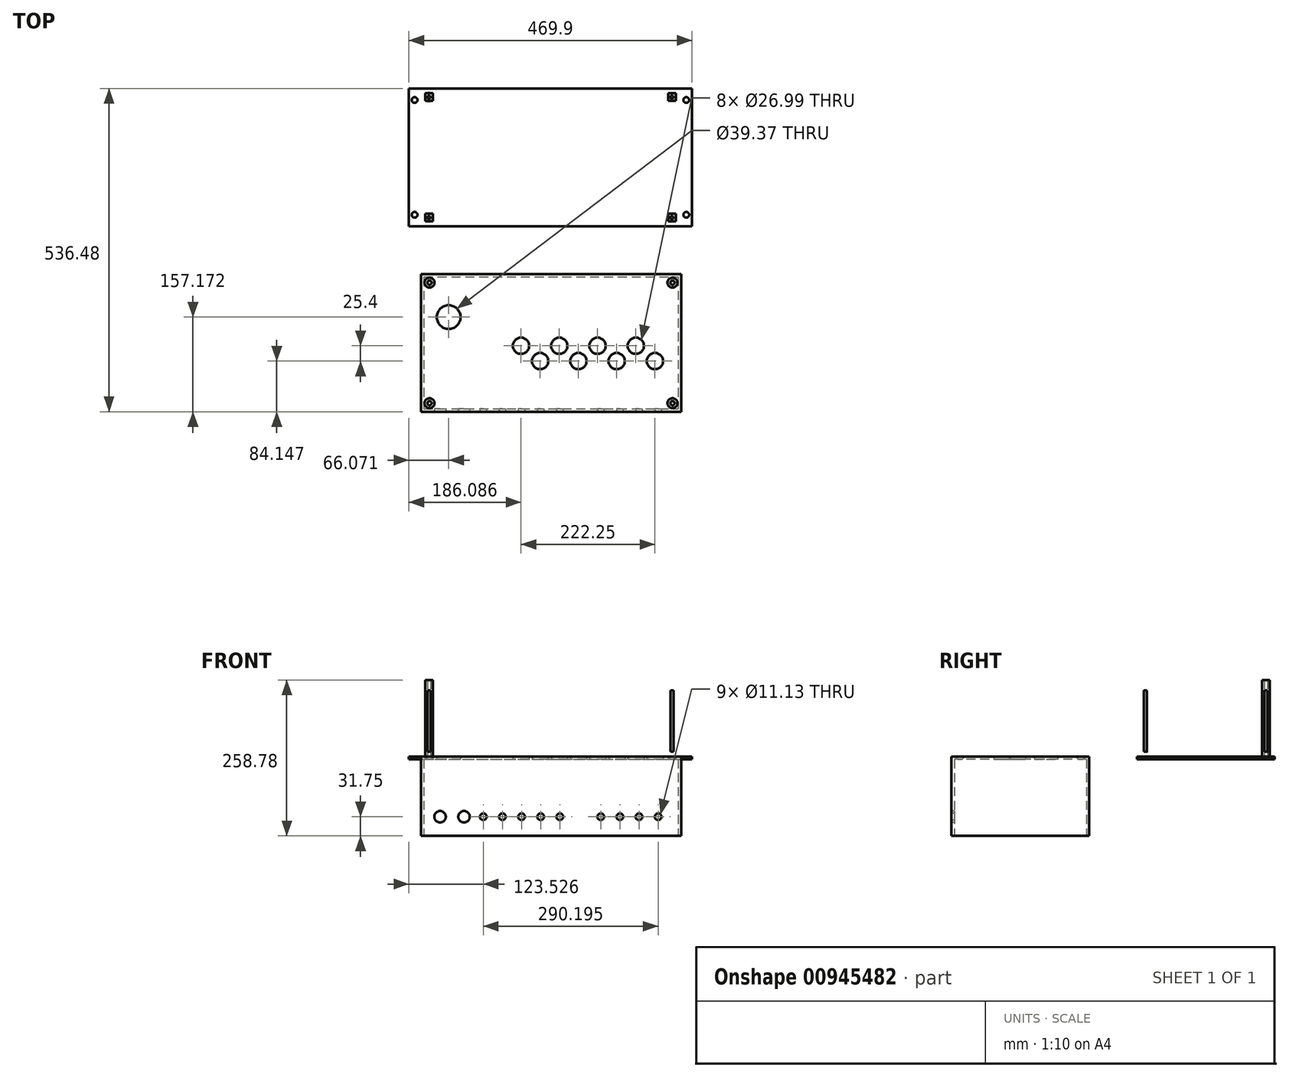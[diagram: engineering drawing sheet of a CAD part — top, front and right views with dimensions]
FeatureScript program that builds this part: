
annotation { "Feature Type Name" : "Feature", "Feature Type Description" : "" }
export const myFeature = defineFeature(function(context is Context, id is Id, definition is map)
    precondition{}
    {
        {
            var Q0;
            Q0=qCreatedBy(makeId("Top.planeOp"),FACE);
            var sketch = newSketch(context, id + "F0", { "sketchPlane" : qUnion([Q0])});
            skLineSegment(sketch, "E0.bottom", {"start": v(-225.5, 123.74) * mm, "end": v(206.3, 123.74) * mm});
            skLineSegment(sketch, "E0.top", {"start": v(-225.5, -104.86) * mm, "end": v(206.3, -104.86) * mm});
            skLineSegment(sketch, "E0.left", {"start": v(-225.5, 123.74) * mm, "end": v(-225.5, -104.86) * mm});
            skLineSegment(sketch, "E0.right", {"start": v(206.3, 123.74) * mm, "end": v(206.3, -104.86) * mm});
            skLineSegment(sketch, "E1.bottom", {"start": v(-220.72, 118.97) * mm, "end": v(201.56, 118.97) * mm});
            skLineSegment(sketch, "E1.top", {"start": v(-220.72, -100.1) * mm, "end": v(201.56, -100.1) * mm});
            skLineSegment(sketch, "E1.left", {"start": v(-220.72, 118.97) * mm, "end": v(-220.72, -100.1) * mm});
            skLineSegment(sketch, "E1.right", {"start": v(201.56, 118.97) * mm, "end": v(201.56, -100.1) * mm});
            skLineSegment(sketch, "E2.bottom", {"start": v(-225.5, 123.74) * mm, "end": v(-244.54, 123.74) * mm});
            skLineSegment(sketch, "E2.top", {"start": v(-225.5, -104.86) * mm, "end": v(-244.54, -104.86) * mm});
            skLineSegment(sketch, "E2.right", {"start": v(-244.54, 123.74) * mm, "end": v(-244.54, -104.86) * mm});
            skLineSegment(sketch, "E3.bottom", {"start": v(206.3, 123.74) * mm, "end": v(225.36, 123.74) * mm});
            skLineSegment(sketch, "E3.top", {"start": v(206.3, -104.86) * mm, "end": v(225.36, -104.86) * mm});
            skLineSegment(sketch, "E3.right", {"start": v(225.36, 123.74) * mm, "end": v(225.36, -104.86) * mm});
            skCircle(sketch, "E4", {"center": v(-235.02, 104.69) * mm, "radius": 4.76 * mm});
            skCircle(sketch, "E5", {"center": v(-235.02, -85.81) * mm, "radius": 4.76 * mm});
            skCircle(sketch, "E6", {"center": v(215.83, 104.69) * mm, "radius": 4.76 * mm});
            skCircle(sketch, "E7", {"center": v(215.83, -85.81) * mm, "radius": 4.76 * mm});
            skLineSegment(sketch, "E8.bottom", {"start": v(-219.74, -188.9) * mm, "end": v(202.53, -188.9) * mm});
            skLineSegment(sketch, "E8.top", {"start": v(-219.74, -407.97) * mm, "end": v(202.53, -407.97) * mm});
            skLineSegment(sketch, "E8.left", {"start": v(-219.74, -188.9) * mm, "end": v(-219.74, -407.97) * mm});
            skLineSegment(sketch, "E8.right", {"start": v(202.53, -188.9) * mm, "end": v(202.53, -407.97) * mm});
            skCircle(sketch, "E9", {"center": v(-58.45, -303.2) * mm, "radius": 13.5 * mm});
            skCircle(sketch, "E10", {"center": v(-26.7, -328.6) * mm, "radius": 13.5 * mm});
            skCircle(sketch, "E11", {"center": v(5.05, -303.2) * mm, "radius": 13.5 * mm});
            skCircle(sketch, "E12", {"center": v(163.8, -328.6) * mm, "radius": 13.5 * mm});
            skCircle(sketch, "E13", {"center": v(100.3, -328.6) * mm, "radius": 13.5 * mm});
            skCircle(sketch, "E14", {"center": v(68.55, -303.2) * mm, "radius": 13.5 * mm});
            skCircle(sketch, "E15", {"center": v(36.8, -328.6) * mm, "radius": 13.5 * mm});
            skCircle(sketch, "E16", {"center": v(132.05, -303.2) * mm, "radius": 13.5 * mm});
            skCircle(sketch, "E17", {"center": v(-178.47, -255.57) * mm, "radius": 19.69 * mm});
            skCircle(sketch, "E18", {"center": v(-210.22, -198.42) * mm, "radius": 3.18 * mm});
            skLineSegment(sketch, "E19.bottom", {"start": v(-217.54, -84.23) * mm, "end": v(-204.84, -84.23) * mm});
            skLineSegment(sketch, "E19.top", {"start": v(-217.54, -96.93) * mm, "end": v(-204.84, -96.93) * mm});
            skLineSegment(sketch, "E19.left", {"start": v(-217.54, -84.23) * mm, "end": v(-217.54, -96.93) * mm});
            skLineSegment(sketch, "E19.right", {"start": v(-204.84, -84.23) * mm, "end": v(-204.84, -96.93) * mm});
            skLineSegment(sketch, "E20.bottom", {"start": v(185.68, -84.23) * mm, "end": v(198.38, -84.23) * mm});
            skLineSegment(sketch, "E20.top", {"start": v(185.68, -96.93) * mm, "end": v(198.38, -96.93) * mm});
            skLineSegment(sketch, "E20.left", {"start": v(185.68, -84.23) * mm, "end": v(185.68, -96.93) * mm});
            skLineSegment(sketch, "E20.right", {"start": v(198.38, -84.23) * mm, "end": v(198.38, -96.93) * mm});
            skLineSegment(sketch, "E21.bottom", {"start": v(185.68, 115.8) * mm, "end": v(198.38, 115.8) * mm});
            skLineSegment(sketch, "E21.top", {"start": v(185.68, 103.1) * mm, "end": v(198.38, 103.1) * mm});
            skLineSegment(sketch, "E21.left", {"start": v(185.68, 115.8) * mm, "end": v(185.68, 103.1) * mm});
            skLineSegment(sketch, "E21.right", {"start": v(198.38, 115.8) * mm, "end": v(198.38, 103.1) * mm});
            skLineSegment(sketch, "E22.bottom", {"start": v(-217.54, 115.8) * mm, "end": v(-204.84, 115.8) * mm});
            skLineSegment(sketch, "E22.top", {"start": v(-217.54, 103.1) * mm, "end": v(-204.84, 103.1) * mm});
            skLineSegment(sketch, "E22.left", {"start": v(-217.54, 115.8) * mm, "end": v(-217.54, 103.1) * mm});
            skLineSegment(sketch, "E22.right", {"start": v(-204.84, 115.8) * mm, "end": v(-204.84, 103.1) * mm});
            skCircle(sketch, "E23", {"center": v(-210.22, -398.44) * mm, "radius": 3.18 * mm});
            skCircle(sketch, "E24", {"center": v(193, -398.44) * mm, "radius": 3.18 * mm});
            skCircle(sketch, "E25", {"center": v(193, -198.42) * mm, "radius": 3.18 * mm});
            skLineSegment(sketch, "E26.bottom", {"start": v(-224.52, -184.14) * mm, "end": v(207.28, -184.14) * mm});
            skLineSegment(sketch, "E26.top", {"start": v(-224.52, -412.74) * mm, "end": v(207.28, -412.74) * mm});
            skLineSegment(sketch, "E26.left", {"start": v(-224.52, -184.14) * mm, "end": v(-224.52, -412.74) * mm});
            skLineSegment(sketch, "E26.right", {"start": v(207.28, -184.14) * mm, "end": v(207.28, -412.74) * mm});
            skCircle(sketch, "E27", {"center": v(-211.2, 109.45) * mm, "radius": 2.58 * mm});
            skCircle(sketch, "E28", {"center": v(192.03, 109.45) * mm, "radius": 2.58 * mm});
            skCircle(sketch, "E29", {"center": v(192.03, -90.58) * mm, "radius": 2.58 * mm});
            skCircle(sketch, "E30", {"center": v(-211.2, -90.58) * mm, "radius": 2.58 * mm});
            skSolve(sketch);
        }
        {
            var Q0;
            Q0=makeQuery(id+"F0.imprint","IMPRINT",FACE,{"disambiguationData":[TD([[makeQuery(id+"F0.imprint","IMPRINT",EDGE,{"derivedFrom":sQuery(id+"F0.wireOp",EDGE,"E1.bottom")}),-1.0]])]});
            var Q1;
            Q1=makeQuery(id+"F0.imprint","IMPRINT",FACE,{"disambiguationData":[TD([[makeQuery(id+"F0.imprint","IMPRINT",EDGE,{"derivedFrom":sQuery(id+"F0.wireOp",EDGE,"E0.bottom")}),-1.0]])]});
            extrude(context, id + "F1", {"entities" : qUnion([Q0, Q1]), "depth" : 4.78 * mm, "offsetDistance" : 25.4 * mm});
        }
        {
            var Q0;
            Q0=makeQuery(id+"F0.imprint","IMPRINT",FACE,{"disambiguationData":[TD([[makeQuery(id+"F0.imprint","IMPRINT",EDGE,{"derivedFrom":sQuery(id+"F0.wireOp",EDGE,"E2.bottom")}),1.0]])]});
            var Q1;
            Q1=makeQuery(id+"F0.imprint","IMPRINT",FACE,{"disambiguationData":[TD([[makeQuery(id+"F0.imprint","IMPRINT",EDGE,{"derivedFrom":sQuery(id+"F0.wireOp",EDGE,"E3.bottom")}),-1.0]])]});
            extrude(context, id + "F2", {"entities" : qUnion([Q0, Q1]), "operationType" : NewBodyOperationType.ADD, "depth" : 4.78 * mm, "offsetDistance" : 25.4 * mm});
        }
        {
            var Q0;
            Q0=makeQuery(id+"F0.imprint","IMPRINT",FACE,{"disambiguationData":[TD([[makeQuery(id+"F0.imprint","IMPRINT",EDGE,{"derivedFrom":sQuery(id+"F0.wireOp",EDGE,"E8.bottom")}),-1.0]])]});
            extrude(context, id + "F3", {"entities" : qUnion([Q0]), "depth" : 4.78 * mm, "offsetDistance" : 25.4 * mm});
        }
        {
            var Q0;
            Q0=makeQuery(id+"F0.imprint","IMPRINT",FACE,{"disambiguationData":[TD([[makeQuery(id+"F0.imprint","IMPRINT",EDGE,{"derivedFrom":sQuery(id+"F0.wireOp",EDGE,"E8.bottom")}),1.0]])]});
            extrude(context, id + "F4", {"entities" : qUnion([Q0]), "operationType" : NewBodyOperationType.ADD, "depth" : 4.78 * mm, "offsetDistance" : 25.4 * mm, "hasSecondDirection" : true, "secondDirectionOppositeDirection" : true, "secondDirectionDepth" : 127 * mm});
        }
        {
            var Q0;
            Q0=makeQuery(id+"F4.opExtrude","SWEPT_FACE",FACE,{"disambiguationData":[OSD([sQuery(id+"F0.wireOp",EDGE,"E26.top")])]});
            var sketch = newSketch(context, id + "F5", { "sketchPlane" : qUnion([Q0])});
            skCircle(sketch, "E31", {"center": v(-192.77, -95.25) * mm, "radius": 9.53 * mm});
            skCircle(sketch, "E32", {"center": v(-153.07, -95.25) * mm, "radius": 9.53 * mm});
            skCircle(sketch, "E33", {"center": v(-89.26, -95.25) * mm, "radius": 5.56 * mm});
            skCircle(sketch, "E34", {"center": v(-57.51, -95.25) * mm, "radius": 5.56 * mm});
            skCircle(sketch, "E35", {"center": v(-25.76, -95.25) * mm, "radius": 5.56 * mm});
            skPoint(sketch, "E36", {"position": v(5.99, -95.25) * mm});
            skCircle(sketch, "E37", {"center": v(5.99, -95.25) * mm, "radius": 5.56 * mm});
            skCircle(sketch, "E38", {"center": v(73.93, -95.25) * mm, "radius": 5.56 * mm});
            skCircle(sketch, "E39", {"center": v(105.68, -95.25) * mm, "radius": 5.56 * mm});
            skCircle(sketch, "E40", {"center": v(137.43, -95.25) * mm, "radius": 5.56 * mm});
            skCircle(sketch, "E41", {"center": v(169.18, -95.25) * mm, "radius": 5.56 * mm});
            skCircle(sketch, "E42", {"center": v(-121.01, -95.25) * mm, "radius": 5.56 * mm});
            skSolve(sketch);
        }
        {
            var Q0;
            Q0=sQuery(id+"F5.wireOp",VERTEX,"E31.center");
            var Q1;
            Q1=sQuery(id+"F5.wireOp",VERTEX,"E32.center");
            var Q2;
            Q2=makeQuery(id+"F3.opExtrude","SWEPT_BODY",BODY,{"disambiguationData":[OSD([sQuery(id+"F0.wireOp",EDGE,"E8.bottom"),sQuery(id+"F0.wireOp",EDGE,"E8.top"),sQuery(id+"F0.wireOp",EDGE,"E8.left"),sQuery(id+"F0.wireOp",EDGE,"E8.right"),sQuery(id+"F0.wireOp",EDGE,"E9"),sQuery(id+"F0.wireOp",EDGE,"E10"),sQuery(id+"F0.wireOp",EDGE,"E11"),sQuery(id+"F0.wireOp",EDGE,"E12"),sQuery(id+"F0.wireOp",EDGE,"E13"),sQuery(id+"F0.wireOp",EDGE,"E14"),sQuery(id+"F0.wireOp",EDGE,"E15"),sQuery(id+"F0.wireOp",EDGE,"E16"),sQuery(id+"F0.wireOp",EDGE,"E17"),sQuery(id+"F0.wireOp",EDGE,"E18"),sQuery(id+"F0.wireOp",EDGE,"E23"),sQuery(id+"F0.wireOp",EDGE,"E24"),sQuery(id+"F0.wireOp",EDGE,"E25")])]});
            hole(context, id + "F6", {"style" : HoleStyle.SIMPLE, "endStyle" : HoleEndStyle.BLIND, "holeDiameter" : 19.05 * mm, "majorDiameter" : 6.35 * mm, "holeDepth" : 12.7 * mm, "isTappedThrough" : true, "tappedDepth" : 12.7 * mm, "tapClearance" : 3, "locations" : qUnion([Q0, Q1]), "scope" : qUnion([Q2])});
        }
        {
            var Q0;
            Q0=sQuery(id+"F5.wireOp",VERTEX,"E33.center");
            var Q1;
            Q1=sQuery(id+"F5.wireOp",VERTEX,"E34.center");
            var Q2;
            Q2=sQuery(id+"F5.wireOp",VERTEX,"E35.center");
            var Q3;
            Q3=sQuery(id+"F5.wireOp",VERTEX,"E36");
            var Q4;
            Q4=sQuery(id+"F5.wireOp",VERTEX,"E38.center");
            var Q5;
            Q5=sQuery(id+"F5.wireOp",VERTEX,"E39.center");
            var Q6;
            Q6=sQuery(id+"F5.wireOp",VERTEX,"E40.center");
            var Q7;
            Q7=sQuery(id+"F5.wireOp",VERTEX,"E41.center");
            var Q8;
            Q8=makeQuery(id+"F3.opExtrude","SWEPT_BODY",BODY,{"disambiguationData":[OSD([sQuery(id+"F0.wireOp",EDGE,"E8.bottom"),sQuery(id+"F0.wireOp",EDGE,"E8.top"),sQuery(id+"F0.wireOp",EDGE,"E8.left"),sQuery(id+"F0.wireOp",EDGE,"E8.right"),sQuery(id+"F0.wireOp",EDGE,"E9"),sQuery(id+"F0.wireOp",EDGE,"E10"),sQuery(id+"F0.wireOp",EDGE,"E11"),sQuery(id+"F0.wireOp",EDGE,"E12"),sQuery(id+"F0.wireOp",EDGE,"E13"),sQuery(id+"F0.wireOp",EDGE,"E14"),sQuery(id+"F0.wireOp",EDGE,"E15"),sQuery(id+"F0.wireOp",EDGE,"E16"),sQuery(id+"F0.wireOp",EDGE,"E17"),sQuery(id+"F0.wireOp",EDGE,"E18"),sQuery(id+"F0.wireOp",EDGE,"E23"),sQuery(id+"F0.wireOp",EDGE,"E24"),sQuery(id+"F0.wireOp",EDGE,"E25")])]});
            hole(context, id + "F7", {"style" : HoleStyle.SIMPLE, "endStyle" : HoleEndStyle.BLIND, "holeDiameter" : 11.13 * mm, "majorDiameter" : 6.35 * mm, "holeDepth" : 12.7 * mm, "isTappedThrough" : true, "tappedDepth" : 12.7 * mm, "tapClearance" : 3, "locations" : qUnion([Q0, Q1, Q2, Q3, Q4, Q5, Q6, Q7]), "scope" : qUnion([Q8])});
        }
        {
            var Q0;
            Q0=makeQuery(id+"F3.opExtrude","CAP_EDGE",EDGE,{"disambiguationData":[OSD([sQuery(id+"F0.wireOp",EDGE,"E23")])],"isStart":false});
            var Q1;
            Q1=makeQuery(id+"F3.opExtrude","CAP_EDGE",EDGE,{"disambiguationData":[OSD([sQuery(id+"F0.wireOp",EDGE,"E18")])],"isStart":false});
            var Q2;
            Q2=makeQuery(id+"F3.opExtrude","CAP_EDGE",EDGE,{"disambiguationData":[OSD([sQuery(id+"F0.wireOp",EDGE,"E25")])],"isStart":false});
            var Q3;
            Q3=makeQuery(id+"F3.opExtrude","CAP_EDGE",EDGE,{"disambiguationData":[OSD([sQuery(id+"F0.wireOp",EDGE,"E24")])],"isStart":false});
            chamfer(context, id + "F8", {"entities" : qUnion([Q0, Q1, Q2, Q3]), "width" : 5.08 * mm, "tangentPropagation" : true});
        }
        {
            var Q0;
            Q0=sQuery(id+"F5.wireOp",VERTEX,"E42.center");
            var Q1;
            Q1=makeQuery(id+"F3.opExtrude","SWEPT_BODY",BODY,{"disambiguationData":[OSD([sQuery(id+"F0.wireOp",EDGE,"E8.bottom"),sQuery(id+"F0.wireOp",EDGE,"E8.top"),sQuery(id+"F0.wireOp",EDGE,"E8.left"),sQuery(id+"F0.wireOp",EDGE,"E8.right"),sQuery(id+"F0.wireOp",EDGE,"E9"),sQuery(id+"F0.wireOp",EDGE,"E10"),sQuery(id+"F0.wireOp",EDGE,"E11"),sQuery(id+"F0.wireOp",EDGE,"E12"),sQuery(id+"F0.wireOp",EDGE,"E13"),sQuery(id+"F0.wireOp",EDGE,"E14"),sQuery(id+"F0.wireOp",EDGE,"E15"),sQuery(id+"F0.wireOp",EDGE,"E16"),sQuery(id+"F0.wireOp",EDGE,"E17"),sQuery(id+"F0.wireOp",EDGE,"E18"),sQuery(id+"F0.wireOp",EDGE,"E23"),sQuery(id+"F0.wireOp",EDGE,"E24"),sQuery(id+"F0.wireOp",EDGE,"E25")])]});
            hole(context, id + "F9", {"style" : HoleStyle.SIMPLE, "endStyle" : HoleEndStyle.BLIND, "holeDiameter" : 11.13 * mm, "majorDiameter" : 6.35 * mm, "holeDepth" : 12.7 * mm, "isTappedThrough" : true, "tappedDepth" : 12.7 * mm, "tapClearance" : 3, "locations" : qUnion([Q0]), "scope" : qUnion([Q1])});
        }
        {
            var Q0;
            Q0=makeQuery(id+"F0.imprint","IMPRINT",FACE,{"disambiguationData":[TD([[makeQuery(id+"F0.imprint","IMPRINT",EDGE,{"derivedFrom":sQuery(id+"F0.wireOp",EDGE,"E22.bottom")}),-1.0]])]});
            var Q1;
            Q1=makeQuery(id+"F0.imprint","IMPRINT",FACE,{"disambiguationData":[TD([[makeQuery(id+"F0.imprint","IMPRINT",EDGE,{"derivedFrom":sQuery(id+"F0.wireOp",EDGE,"E19.bottom")}),-1.0]])]});
            var Q2;
            Q2=makeQuery(id+"F0.imprint","IMPRINT",FACE,{"disambiguationData":[TD([[makeQuery(id+"F0.imprint","IMPRINT",EDGE,{"derivedFrom":sQuery(id+"F0.wireOp",EDGE,"E21.bottom")}),-1.0]])]});
            var Q3;
            Q3=makeQuery(id+"F0.imprint","IMPRINT",FACE,{"disambiguationData":[TD([[makeQuery(id+"F0.imprint","IMPRINT",EDGE,{"derivedFrom":sQuery(id+"F0.wireOp",EDGE,"E20.bottom")}),-1.0]])]});
            extrude(context, id + "F10", {"entities" : qUnion([Q0, Q1, Q2, Q3]), "operationType" : NewBodyOperationType.ADD, "depth" : 131.78 * mm, "offsetDistance" : 25.4 * mm});
        }
        {
            var Q0;
            Q0=makeQuery(id+"F0.imprint","IMPRINT",FACE,{"disambiguationData":[TD([[makeQuery(id+"F0.imprint","IMPRINT",EDGE,{"derivedFrom":sQuery(id+"F0.wireOp",EDGE,"E29")}),1.0]])]});
            var Q1;
            Q1=makeQuery(id+"F0.imprint","IMPRINT",FACE,{"disambiguationData":[TD([[makeQuery(id+"F0.imprint","IMPRINT",EDGE,{"derivedFrom":sQuery(id+"F0.wireOp",EDGE,"E28")}),1.0]])]});
            var Q2;
            Q2=makeQuery(id+"F0.imprint","IMPRINT",FACE,{"disambiguationData":[TD([[makeQuery(id+"F0.imprint","IMPRINT",EDGE,{"derivedFrom":sQuery(id+"F0.wireOp",EDGE,"E30")}),1.0]])]});
            var Q3;
            Q3=makeQuery(id+"F0.imprint","IMPRINT",FACE,{"disambiguationData":[TD([[makeQuery(id+"F0.imprint","IMPRINT",EDGE,{"derivedFrom":sQuery(id+"F0.wireOp",EDGE,"E27")}),1.0]])]});
            extrude(context, id + "F11", {"entities" : qUnion([Q0, Q1, Q2, Q3]), "depth" : 101.6 * mm, "offsetDistance" : 25.4 * mm});
        }
        {
            var Q0;
            Q0=makeQuery(id+"F11.opExtrude","SWEPT_BODY",BODY,{"disambiguationData":[OSD([sQuery(id+"F0.wireOp",EDGE,"E27")])]});
            var Q1;
            Q1=makeQuery(id+"F11.opExtrude","SWEPT_BODY",BODY,{"disambiguationData":[OSD([sQuery(id+"F0.wireOp",EDGE,"E30")])]});
            var Q2;
            Q2=makeQuery(id+"F11.opExtrude","SWEPT_BODY",BODY,{"disambiguationData":[OSD([sQuery(id+"F0.wireOp",EDGE,"E29")])]});
            var Q3;
            Q3=makeQuery(id+"F11.opExtrude","SWEPT_BODY",BODY,{"disambiguationData":[OSD([sQuery(id+"F0.wireOp",EDGE,"E28")])]});
            transform(context, id + "F12", {"entities" : qUnion([Q0, Q1, Q2, Q3]), "transformType" : TransformType.TRANSLATION_3D, "dx" : 0 * mm, "dy" : 0 * mm, "dz" : 12.7 * mm, "makeCopy" : false});
        }
        {
            var Q0;
            Q0=makeQuery(id+"F10.opExtrude","CAP_EDGE",EDGE,{"disambiguationData":[OSD([sQuery(id+"F0.wireOp",EDGE,"E30")])],"isStart":true});
            var Q1;
            Q1=makeQuery(id+"F10.opExtrude","CAP_EDGE",EDGE,{"disambiguationData":[OSD([sQuery(id+"F0.wireOp",EDGE,"E29")])],"isStart":true});
            var Q2;
            Q2=makeQuery(id+"F10.opExtrude","CAP_EDGE",EDGE,{"disambiguationData":[OSD([sQuery(id+"F0.wireOp",EDGE,"E28")])],"isStart":true});
            var Q3;
            Q3=makeQuery(id+"F10.opExtrude","CAP_EDGE",EDGE,{"disambiguationData":[OSD([sQuery(id+"F0.wireOp",EDGE,"E27")])],"isStart":true});
            chamfer(context, id + "F13", {"entities" : qUnion([Q0, Q1, Q2, Q3]), "width" : 5.08 * mm, "tangentPropagation" : true});
        }
    });
